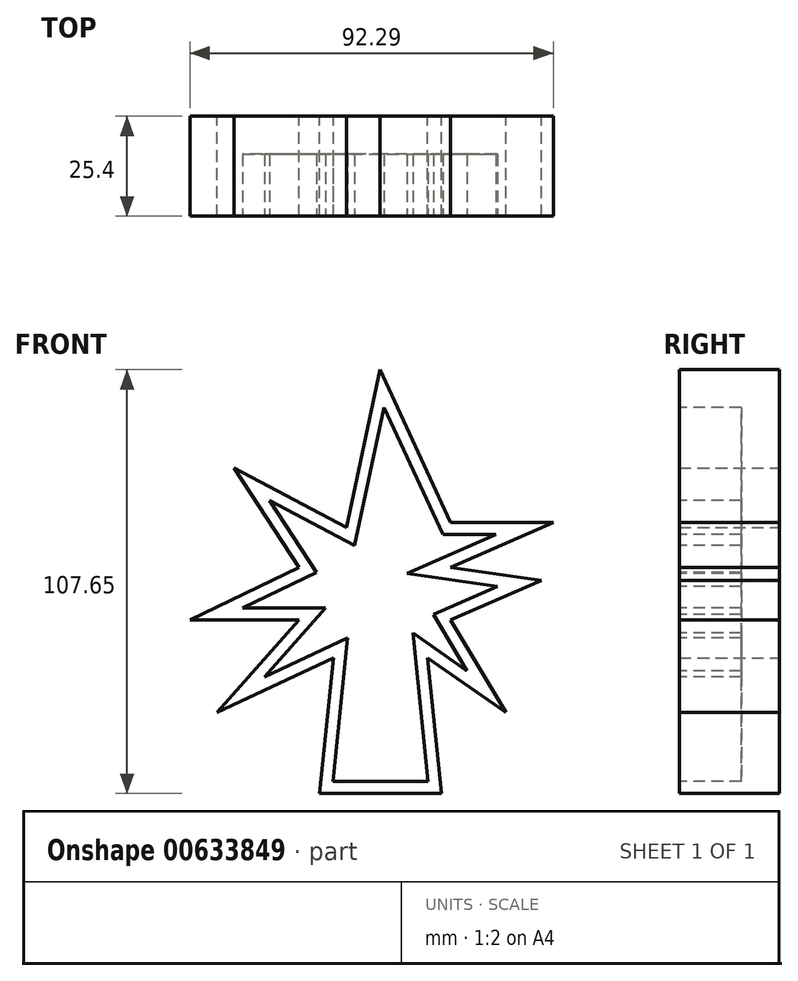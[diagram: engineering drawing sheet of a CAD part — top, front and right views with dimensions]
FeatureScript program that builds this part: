
annotation { "Feature Type Name" : "Feature", "Feature Type Description" : "" }
export const myFeature = defineFeature(function(context is Context, id is Id, definition is map)
    precondition{}
    {
        {
            var Q0;
            Q0=qCreatedBy(makeId("Front.planeOp"),FACE);
            var sketch = newSketch(context, id + "F0", { "sketchPlane" : qUnion([Q0])});
            skLineSegment(sketch, "E0", {"start": v(0, 50.28) * mm, "end": v(-8.56, 10.16) * mm});
            skLineSegment(sketch, "E1", {"start": v(-8.56, 10.16) * mm, "end": v(-37.06, 25.28) * mm});
            skLineSegment(sketch, "E2", {"start": v(-37.06, 25.28) * mm, "end": v(-20.62, 0) * mm});
            skLineSegment(sketch, "E3", {"start": v(-20.62, 0) * mm, "end": v(-48.24, -13.3) * mm});
            skLineSegment(sketch, "E4", {"start": v(-48.24, -13.3) * mm, "end": v(-20.62, -13.3) * mm});
            skLineSegment(sketch, "E5", {"start": v(-20.62, -13.3) * mm, "end": v(-41.44, -36.76) * mm});
            skLineSegment(sketch, "E6", {"start": v(-41.44, -36.76) * mm, "end": v(-11.85, -22.95) * mm});
            skLineSegment(sketch, "E7", {"start": v(-11.85, -22.95) * mm, "end": v(-15.35, -57.37) * mm});
            skLineSegment(sketch, "E8", {"start": v(-15.35, -57.37) * mm, "end": v(15.56, -57.37) * mm});
            skLineSegment(sketch, "E9", {"start": v(15.56, -57.37) * mm, "end": v(12.05, -22.95) * mm});
            skLineSegment(sketch, "E10", {"start": v(12.05, -22.95) * mm, "end": v(32, -36.76) * mm});
            skLineSegment(sketch, "E11", {"start": v(32, -36.76) * mm, "end": v(17.97, -13.3) * mm});
            skLineSegment(sketch, "E12", {"start": v(17.97, -13.3) * mm, "end": v(40.99, -3.22) * mm});
            skLineSegment(sketch, "E13", {"start": v(40.99, -3.22) * mm, "end": v(17.97, 0) * mm});
            skLineSegment(sketch, "E14", {"start": v(17.97, 0) * mm, "end": v(44.05, 11.43) * mm});
            skLineSegment(sketch, "E15", {"start": v(44.05, 11.43) * mm, "end": v(17.97, 11.43) * mm});
            skLineSegment(sketch, "E16", {"start": v(17.97, 11.43) * mm, "end": v(0, 50.28) * mm});
            skSolve(sketch);
        }
        {
            var Q0;
            Q0=makeQuery(id+"F0.imprint","IMPRINT",FACE,{"disambiguationData":[TD([[makeQuery(id+"F0.imprint","IMPRINT",EDGE,{"derivedFrom":sQuery(id+"F0.wireOp",EDGE,"E0")}),1.0]])]});
            extrude(context, id + "F1", {"entities" : qUnion([Q0]), "depth" : 25.4 * mm, "offsetDistance" : 25.4 * mm});
        }
        {
            var Q0;
            Q0=makeQuery(id+"F1.opExtrude","CAP_FACE",FACE,{"disambiguationData":[OSD([sQuery(id+"F0.wireOp",EDGE,"E0"),sQuery(id+"F0.wireOp",EDGE,"E1"),sQuery(id+"F0.wireOp",EDGE,"E2"),sQuery(id+"F0.wireOp",EDGE,"E3"),sQuery(id+"F0.wireOp",EDGE,"E4"),sQuery(id+"F0.wireOp",EDGE,"E5"),sQuery(id+"F0.wireOp",EDGE,"E6"),sQuery(id+"F0.wireOp",EDGE,"E7"),sQuery(id+"F0.wireOp",EDGE,"E8"),sQuery(id+"F0.wireOp",EDGE,"E9"),sQuery(id+"F0.wireOp",EDGE,"E10"),sQuery(id+"F0.wireOp",EDGE,"E11"),sQuery(id+"F0.wireOp",EDGE,"E12"),sQuery(id+"F0.wireOp",EDGE,"E13"),sQuery(id+"F0.wireOp",EDGE,"E14"),sQuery(id+"F0.wireOp",EDGE,"E15"),sQuery(id+"F0.wireOp",EDGE,"E16")])],"isStart":false});
            var sketch = newSketch(context, id + "F2", { "sketchPlane" : qUnion([Q0])});
            skLineSegment(sketch, "E17.0", {"start": v(13.58, -11.9) * mm, "end": v(29.9, -4.75) * mm});
            skLineSegment(sketch, "E17.1", {"start": v(22.15, -26.24) * mm, "end": v(13.58, -11.9) * mm});
            skLineSegment(sketch, "E17.2", {"start": v(8.35, -16.68) * mm, "end": v(22.15, -26.24) * mm});
            skLineSegment(sketch, "E17.3", {"start": v(12.18, -54.32) * mm, "end": v(8.35, -16.68) * mm});
            skLineSegment(sketch, "E17.4", {"start": v(-11.98, -54.32) * mm, "end": v(12.18, -54.32) * mm});
            skLineSegment(sketch, "E17.5", {"start": v(29.9, -4.75) * mm, "end": v(6.88, -1.53) * mm});
            skLineSegment(sketch, "E17.6", {"start": v(-8.27, -17.92) * mm, "end": v(-11.98, -54.32) * mm});
            skLineSegment(sketch, "E17.7", {"start": v(1.07, 40.7) * mm, "end": v(-6.42, 5.57) * mm});
            skLineSegment(sketch, "E17.8", {"start": v(16.02, 8.38) * mm, "end": v(1.07, 40.7) * mm});
            skLineSegment(sketch, "E17.9", {"start": v(29.5, 8.38) * mm, "end": v(16.02, 8.38) * mm});
            skLineSegment(sketch, "E17.10", {"start": v(6.88, -1.53) * mm, "end": v(29.5, 8.38) * mm});
            skLineSegment(sketch, "E17.11", {"start": v(-6.42, 5.57) * mm, "end": v(-28.08, 17.07) * mm});
            skLineSegment(sketch, "E17.12", {"start": v(-28.08, 17.07) * mm, "end": v(-16.17, -1.24) * mm});
            skLineSegment(sketch, "E17.13", {"start": v(-16.17, -1.24) * mm, "end": v(-34.88, -10.25) * mm});
            skLineSegment(sketch, "E17.14", {"start": v(-34.88, -10.25) * mm, "end": v(-13.83, -10.25) * mm});
            skLineSegment(sketch, "E17.15", {"start": v(-13.83, -10.25) * mm, "end": v(-29.39, -27.77) * mm});
            skLineSegment(sketch, "E17.16", {"start": v(-29.39, -27.77) * mm, "end": v(-8.27, -17.92) * mm});
            skSolve(sketch);
        }
        {
            var Q0;
            Q0=makeQuery(id+"F2.imprint","IMPRINT",FACE,{"disambiguationData":[TD([[makeQuery(id+"F2.imprint","IMPRINT",EDGE,{"derivedFrom":sQuery(id+"F2.wireOp",EDGE,"E17.0")}),1.0]])]});
            extrude(context, id + "F3", {"entities" : qUnion([Q0]), "operationType" : NewBodyOperationType.REMOVE, "oppositeDirection" : true, "depth" : 15.75 * mm, "offsetDistance" : 25.4 * mm});
        }
    });
